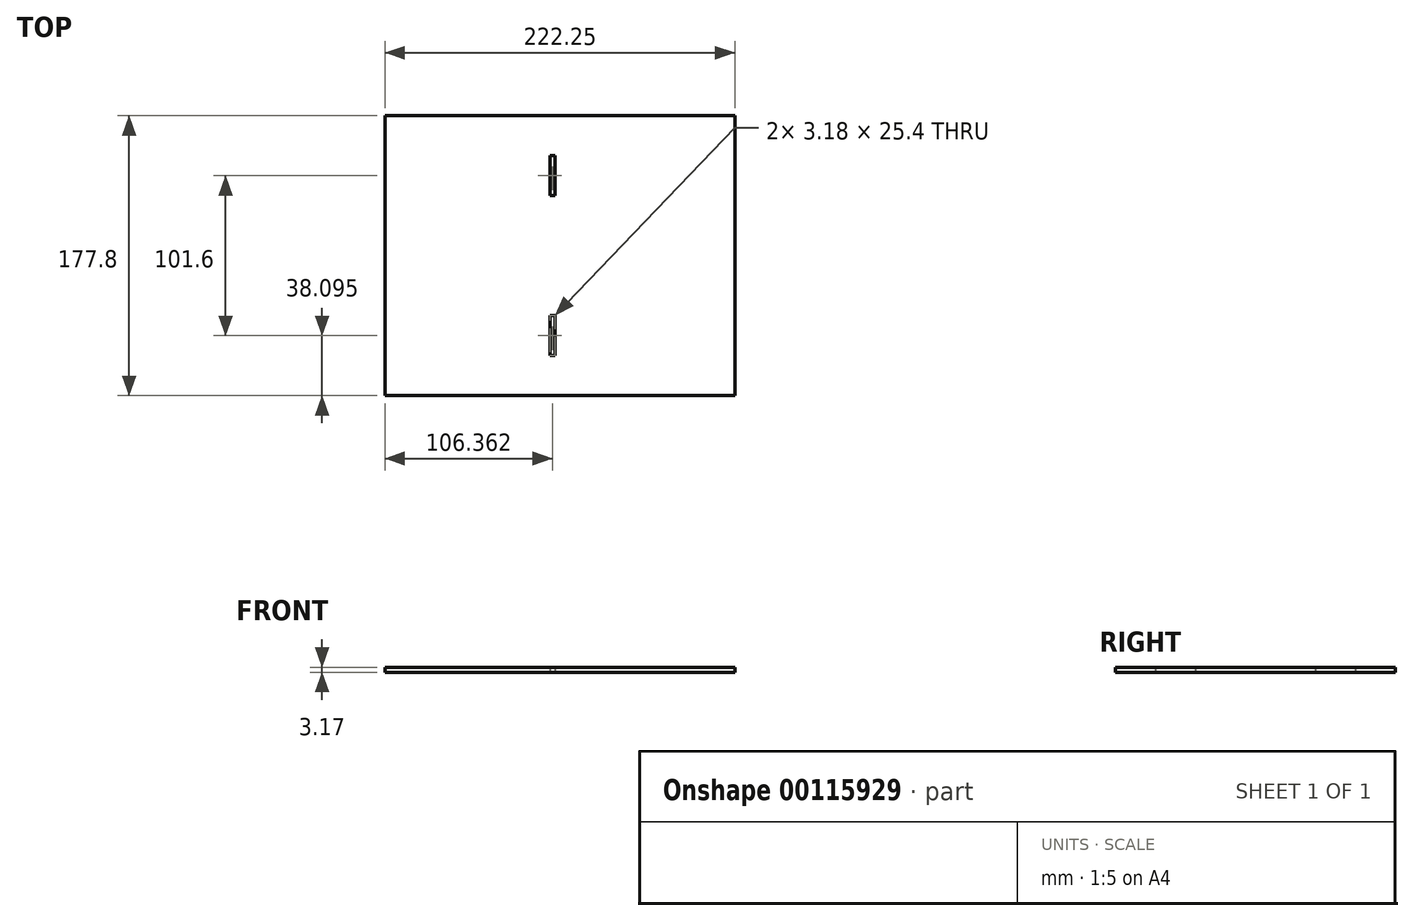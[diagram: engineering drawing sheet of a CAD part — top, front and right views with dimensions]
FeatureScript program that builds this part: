
annotation { "Feature Type Name" : "Feature", "Feature Type Description" : "" }
export const myFeature = defineFeature(function(context is Context, id is Id, definition is map)
    precondition{}
    {
        {
            var Q0;
            Q0=qCreatedBy(makeId("Top.planeOp"),FACE);
            var sketch = newSketch(context, id + "F0", { "sketchPlane" : qUnion([Q0])});
            skLineSegment(sketch, "E0.bottom", {"start": v(-103.28, 85.56) * mm, "end": v(118.97, 85.56) * mm});
            skLineSegment(sketch, "E0.top", {"start": v(-103.28, -92.24) * mm, "end": v(118.97, -92.24) * mm});
            skLineSegment(sketch, "E0.left", {"start": v(-103.28, 85.56) * mm, "end": v(-103.28, -92.24) * mm});
            skLineSegment(sketch, "E0.right", {"start": v(118.97, 85.56) * mm, "end": v(118.97, -92.24) * mm});
            skLineSegment(sketch, "E1.bottom", {"start": v(1.5, 60.16) * mm, "end": v(4.67, 60.16) * mm});
            skLineSegment(sketch, "E1.top", {"start": v(1.5, 34.76) * mm, "end": v(4.67, 34.76) * mm});
            skLineSegment(sketch, "E1.left", {"start": v(1.5, 60.16) * mm, "end": v(1.5, 34.76) * mm});
            skLineSegment(sketch, "E1.right", {"start": v(4.67, 60.16) * mm, "end": v(4.67, 34.76) * mm});
            skLineSegment(sketch, "E2", {"start": v(-103.28, -3.34) * mm, "end": v(118.97, -3.34) * mm});
            skLineSegment(sketch, "E3.MirrorCS", {"start": v(-103.28, -3.34) * mm, "end": v(99.92, -3.34) * mm});
            skLineSegment(sketch, "E4.MirrorCS", {"start": v(1.5, -66.84) * mm, "end": v(1.5, -41.44) * mm});
            skLineSegment(sketch, "E5.MirrorCS", {"start": v(1.5, -41.44) * mm, "end": v(4.67, -41.44) * mm});
            skLineSegment(sketch, "E6.MirrorCS", {"start": v(1.5, -66.84) * mm, "end": v(4.67, -66.84) * mm});
            skLineSegment(sketch, "E7", {"start": v(4.67, -41.44) * mm, "end": v(4.67, -66.84) * mm});
            skSolve(sketch);
        }
        {
            var Q0;
            {var subQ1=sQuery(id+"F0.wireOp",EDGE,"E0.bottom");Q0=makeQuery(id+"F0.imprint","IMPRINT",FACE,{"disambiguationData":[TD([[makeQuery(id+"F0.imprint","IMPRINT",EDGE,{"derivedFrom":subQ1}),-1.0]])]});}
            var Q1;
            {var subQ2=sQuery(id+"F0.wireOp",EDGE,"E0.top");Q1=makeQuery(id+"F0.imprint","IMPRINT",FACE,{"disambiguationData":[TD([[makeQuery(id+"F0.imprint","IMPRINT",EDGE,{"derivedFrom":subQ2}),1.0]])]});}
            extrude(context, id + "F1", {"entities" : qUnion([Q0, Q1]), "depth" : 3.17 * mm});
        }
    });
